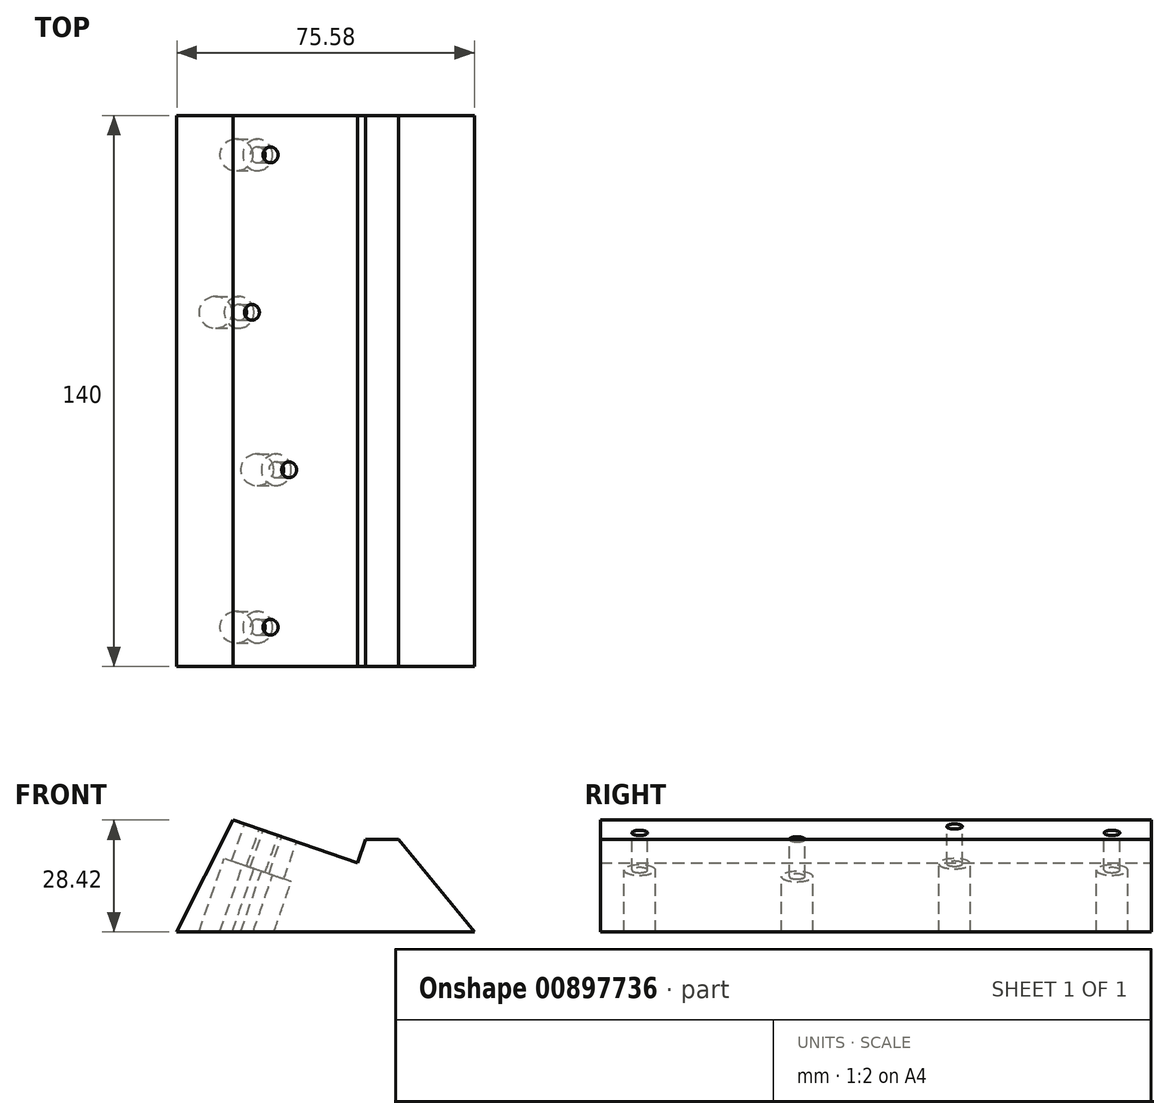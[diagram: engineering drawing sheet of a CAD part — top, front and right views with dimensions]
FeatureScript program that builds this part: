
annotation { "Feature Type Name" : "Feature", "Feature Type Description" : "" }
export const myFeature = defineFeature(function(context is Context, id is Id, definition is map)
    precondition{}
    {
        {
            var Q0;
            Q0=qCreatedBy(makeId("Front.planeOp"),FACE);
            var sketch = newSketch(context, id + "F0", { "sketchPlane" : qUnion([Q0])});
            skLineSegment(sketch, "E0.MirrorCS", {"start": v(0, 0) * mm, "end": v(-31.56, 10.88) * mm});
            skLineSegment(sketch, "E1", {"start": v(0, 0) * mm, "end": v(2.06, 5.98) * mm});
            skLineSegment(sketch, "E2", {"start": v(2.06, 5.98) * mm, "end": v(10.43, 5.98) * mm});
            skLineSegment(sketch, "E3", {"start": v(-31.56, 10.88) * mm, "end": v(-45.91, -17.54) * mm});
            skLineSegment(sketch, "E4", {"start": v(-45.91, -17.54) * mm, "end": v(29.67, -17.54) * mm});
            skLineSegment(sketch, "E5", {"start": v(29.67, -17.54) * mm, "end": v(10.43, 5.98) * mm});
            skSolve(sketch);
        }
        {
            var Q0;
            Q0=makeQuery(id+"F0.imprint","IMPRINT",FACE,{"disambiguationData":[TD([[makeQuery(id+"F0.imprint","IMPRINT",EDGE,{"derivedFrom":sQuery(id+"F0.wireOp",EDGE,"E0.MirrorCS")}),1.0]])]});
            extrude(context, id + "F1", {"entities" : qUnion([Q0]), "depth" : 140 * mm, "offsetDistance" : 25 * mm});
        }
        {
            var Q0;
            Q0=makeQuery(id+"F1.opExtrude","SWEPT_FACE",FACE,{"disambiguationData":[OSD([sQuery(id+"F0.wireOp",EDGE,"E0.MirrorCS")])]});
            var sketch = newSketch(context, id + "F2", { "sketchPlane" : qUnion([Q0])});
            skCircle(sketch, "E6", {"center": v(-23.39, -130) * mm, "radius": 4 * mm});
            skPoint(sketch, "E6.centerSnap0", {"position": v(-16.7, -140) * mm});
            skCircle(sketch, "E7", {"center": v(-23.39, -10) * mm, "radius": 4 * mm});
            skPoint(sketch, "E7.centerSnap0", {"position": v(-16.7, 0) * mm});
            skCircle(sketch, "E8", {"center": v(-28.39, -50) * mm, "radius": 4 * mm});
            skCircle(sketch, "E9", {"center": v(-18.39, -90) * mm, "radius": 4 * mm});
            skSolve(sketch);
        }
        {
            var Q0;
            Q0=makeQuery(id+"F2.imprint","IMPRINT",FACE,{"disambiguationData":[TD([[makeQuery(id+"F2.imprint","IMPRINT",EDGE,{"derivedFrom":sQuery(id+"F2.wireOp",EDGE,"E7")}),1.0]])]});
            var Q1;
            Q1=makeQuery(id+"F2.imprint","IMPRINT",FACE,{"disambiguationData":[TD([[makeQuery(id+"F2.imprint","IMPRINT",EDGE,{"derivedFrom":sQuery(id+"F2.wireOp",EDGE,"E8")}),1.0]])]});
            var Q2;
            Q2=makeQuery(id+"F2.imprint","IMPRINT",FACE,{"disambiguationData":[TD([[makeQuery(id+"F2.imprint","IMPRINT",EDGE,{"derivedFrom":sQuery(id+"F2.wireOp",EDGE,"E6")}),1.0]])]});
            var Q3;
            Q3=makeQuery(id+"F2.imprint","IMPRINT",FACE,{"disambiguationData":[TD([[makeQuery(id+"F2.imprint","IMPRINT",EDGE,{"derivedFrom":sQuery(id+"F2.wireOp",EDGE,"E9")}),1.0]])]});
            extrude(context, id + "F3", {"entities" : qUnion([Q0, Q1, Q2, Q3]), "operationType" : NewBodyOperationType.REMOVE, "oppositeDirection" : true, "depth" : 30 * mm, "offsetDistance" : 25 * mm});
        }
        {
            var Q0;
            Q0=makeQuery(id+"F1.opExtrude","SWEPT_FACE",FACE,{"disambiguationData":[OSD([sQuery(id+"F0.wireOp",EDGE,"E0.MirrorCS")])]});
            var sketch = newSketch(context, id + "F4", { "sketchPlane" : qUnion([Q0])});
            skCircle(sketch, "E10", {"center": v(-23.39, -130) * mm, "radius": 4 * mm});
            skCircle(sketch, "E11", {"center": v(-23.39, -130) * mm, "radius": 2 * mm});
            skCircle(sketch, "E12", {"center": v(-23.39, -10) * mm, "radius": 4 * mm});
            skCircle(sketch, "E13", {"center": v(-23.39, -10) * mm, "radius": 2 * mm});
            skCircle(sketch, "E14", {"center": v(-28.39, -50) * mm, "radius": 4 * mm});
            skCircle(sketch, "E15", {"center": v(-28.39, -50) * mm, "radius": 2 * mm});
            skCircle(sketch, "E16", {"center": v(-18.39, -90) * mm, "radius": 4 * mm});
            skCircle(sketch, "E17", {"center": v(-18.39, -90) * mm, "radius": 2 * mm});
            skSolve(sketch);
        }
        {
            var Q0;
            Q0=makeQuery(id+"F4.imprint","IMPRINT",FACE,{"disambiguationData":[TD([[makeQuery(id+"F4.imprint","IMPRINT",EDGE,{"derivedFrom":sQuery(id+"F4.wireOp",EDGE,"E12")}),1.0]])]});
            var Q1;
            Q1=makeQuery(id+"F4.imprint","IMPRINT",FACE,{"disambiguationData":[TD([[makeQuery(id+"F4.imprint","IMPRINT",EDGE,{"derivedFrom":sQuery(id+"F4.wireOp",EDGE,"E10")}),1.0]])]});
            var Q2;
            Q2=makeQuery(id+"F4.imprint","IMPRINT",FACE,{"disambiguationData":[TD([[makeQuery(id+"F4.imprint","IMPRINT",EDGE,{"derivedFrom":sQuery(id+"F4.wireOp",EDGE,"E14")}),1.0]])]});
            var Q3;
            Q3=makeQuery(id+"F4.imprint","IMPRINT",FACE,{"disambiguationData":[TD([[makeQuery(id+"F4.imprint","IMPRINT",EDGE,{"derivedFrom":sQuery(id+"F4.wireOp",EDGE,"E16")}),1.0]])]});
            extrude(context, id + "F5", {"entities" : qUnion([Q0, Q1, Q2, Q3]), "operationType" : NewBodyOperationType.ADD, "oppositeDirection" : true, "depth" : 10 * mm, "offsetDistance" : 25 * mm});
        }
    });
